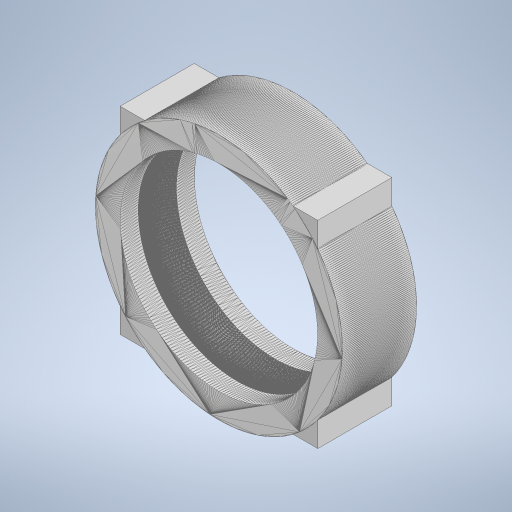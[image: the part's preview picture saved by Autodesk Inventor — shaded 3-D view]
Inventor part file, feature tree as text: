
AUTODESK INVENTOR PART (.ipt)
format: ipt  version: 2024 (Build 280153000, 153)  size: 1,466,880 bytes
history: native  units: mm
features: other x2, extrude x1, sketch x1
ambient origin geometry x8: Origin, YZ Plane, XZ Plane, XY Plane, X Axis, Y Axis, Z Axis, Center Point
bodies: Body1 (feature_tree)
feature tree (4):
  other  "BBbearing2"
  extrude  "押し出し2"  Depth=30.0mm
  sketch  "スケッチ1"
  other  "メッシュ フィーチャ1"
